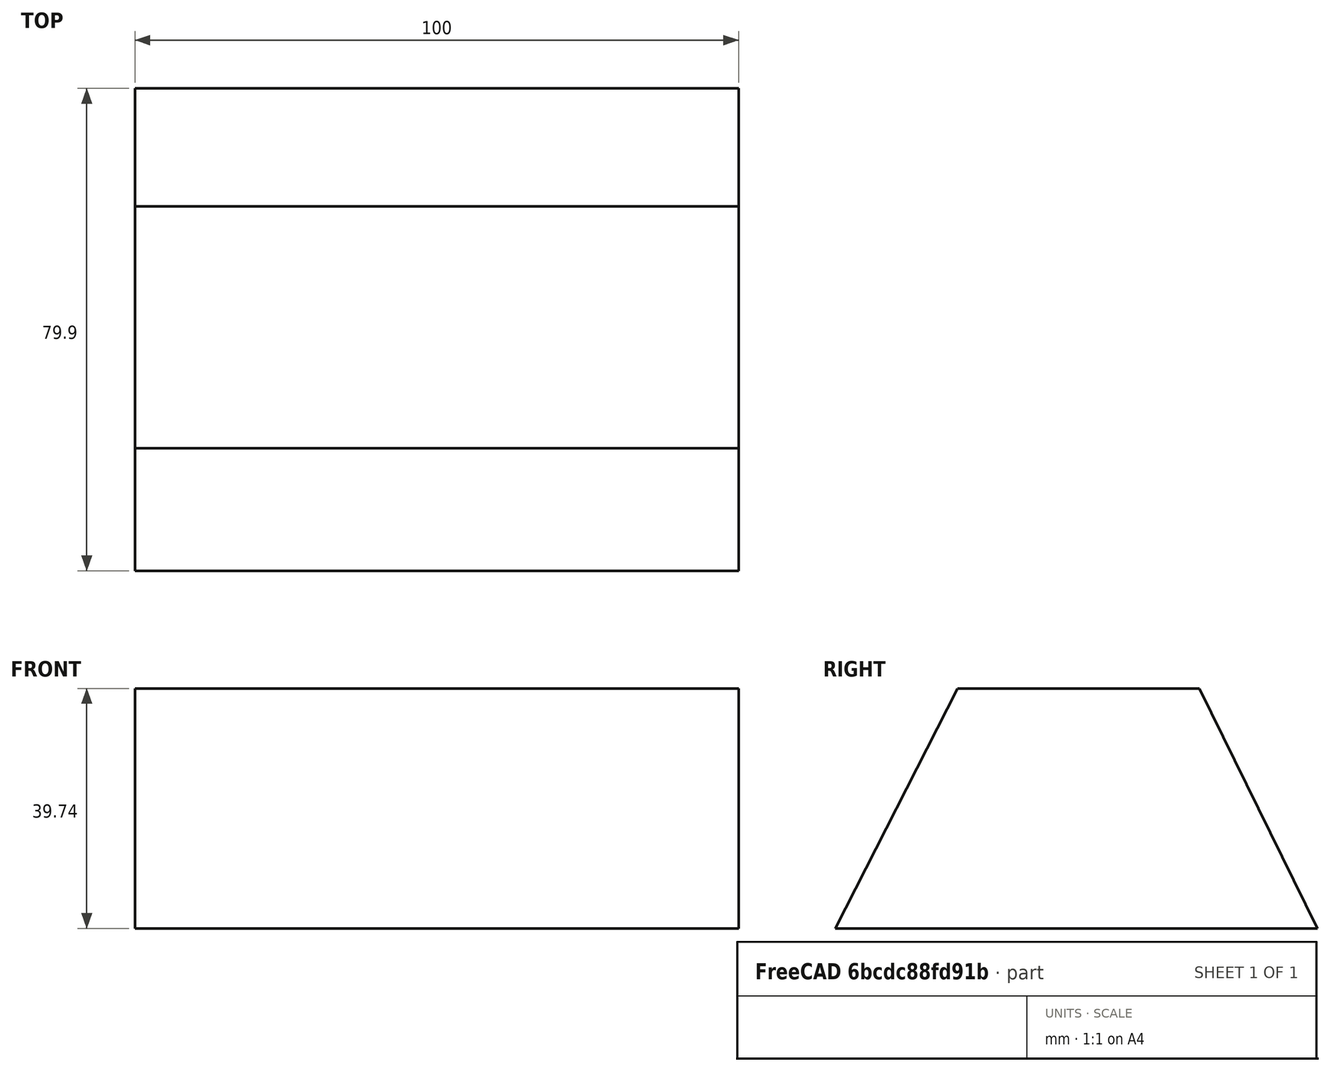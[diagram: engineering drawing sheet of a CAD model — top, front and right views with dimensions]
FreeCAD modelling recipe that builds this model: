
FCSTD DOCUMENT  (FreeCAD 1.0R39319 (Git))
Label: ojt1_t16r01_gold_bar
License: All rights reserved
LicenseURL: https://en.wikipedia.org/wiki/All_rights_reserved
objects: Sketcher::SketchObject×1, PartDesign::Pad×1, PartDesign::Body×1
note: 6 computed .brp shape members not serialized (recipe doc carries the construction recipe); baked Part::Feature solids carry a one-line shape summary decoded from their .brp

FEATURE [Sketcher::SketchObject] Sketch
  ArcFitTolerance = 1e-06
  AttachmentSupport = -> [YZ_Plane]
  FullyConstrained = false
  MakeInternals = false
  MapMode = 5
  Placement = pos=(0,0,0) rot=(0.57735,0.57735,0.57735;2.0944rad)
  sketch-geometry (4):
    g0: LineSegment StartX=-40.1355 StartY=9.952 StartZ=0 EndX=-19.8493 EndY=49.6919 EndZ=0
    g1: LineSegment StartX=-19.8493 StartY=49.6919 StartZ=0 EndX=20.206 EndY=49.6919 EndZ=0
    g2: LineSegment StartX=20.206 StartY=49.6919 StartZ=0 EndX=39.7606 EndY=9.952 EndZ=0
    g3: LineSegment StartX=39.7606 StartY=9.952 StartZ=0 EndX=-40.1355 EndY=9.952 EndZ=0
  constraints (6):
    c: Coincident(g0,g1)
    c: Horizontal(g1)
    c: Coincident(g1,g2)
    c: Coincident(g2,g3)
    c: Coincident(g3,g0)
    c: Horizontal(g3)
FEATURE [PartDesign::Pad] Pad
  Direction = (1,0,0)
  Length = 100
  Length2 = 10
  Placement = pos=(0,0,0) rot=(1,1,1;2.0944rad)
  Profile = -> Sketch
  ReferenceAxis = -> Sketch [N_Axis]
  Refine = true
  Suppressed = false
  Type = 0
FEATURE [PartDesign::Body] Body
  AllowCompound = false
  Group = -> [Sketch,Pad]
  Origin = -> Origin
  Tip = -> Pad
